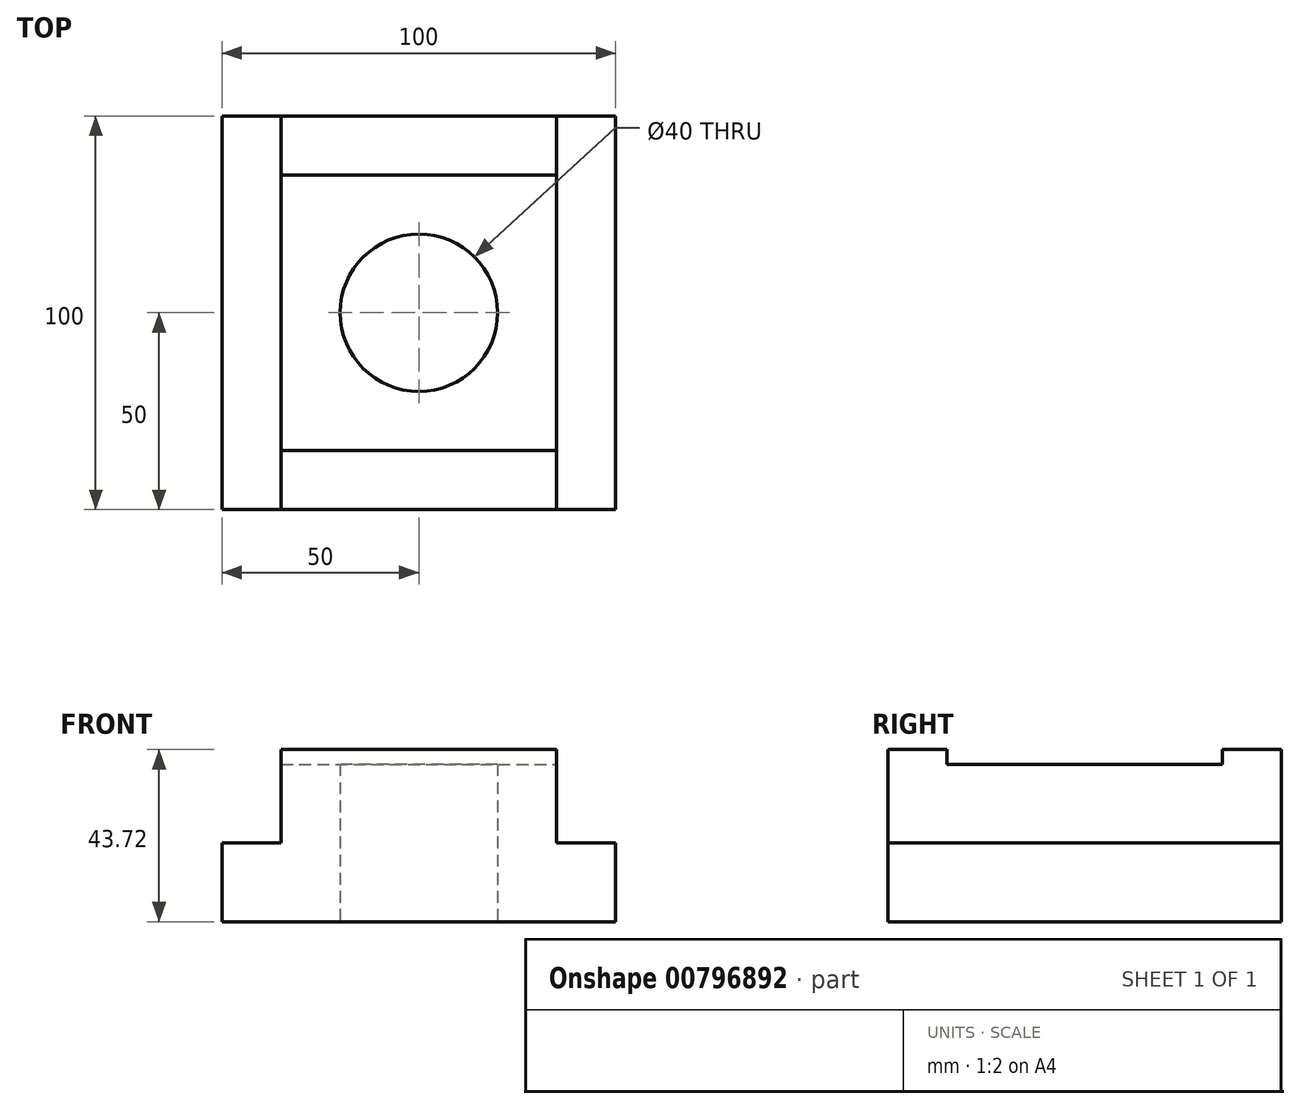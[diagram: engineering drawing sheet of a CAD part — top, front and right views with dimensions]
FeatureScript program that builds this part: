
annotation { "Feature Type Name" : "Feature", "Feature Type Description" : "" }
export const myFeature = defineFeature(function(context is Context, id is Id, definition is map)
    precondition{}
    {
        {
            var Q0;
            Q0=qCreatedBy(makeId("Front.planeOp"),FACE);
            var sketch = newSketch(context, id + "F0", { "sketchPlane" : qUnion([Q0])});
            skLineSegment(sketch, "E0.bottom", {"start": v(0, 0) * mm, "end": v(100, 0) * mm});
            skLineSegment(sketch, "E0.top", {"start": v(0, 20) * mm, "end": v(100, 20) * mm});
            skLineSegment(sketch, "E0.left", {"start": v(0, 0) * mm, "end": v(0, 20) * mm});
            skLineSegment(sketch, "E0.right", {"start": v(100, 0) * mm, "end": v(100, 20) * mm});
            skLineSegment(sketch, "E1.bottom", {"start": v(15, 20) * mm, "end": v(85, 20) * mm});
            skLineSegment(sketch, "E1.top", {"start": v(15, 43.72) * mm, "end": v(85, 43.72) * mm});
            skLineSegment(sketch, "E1.left", {"start": v(15, 20) * mm, "end": v(15, 43.72) * mm});
            skLineSegment(sketch, "E1.right", {"start": v(85, 20) * mm, "end": v(85, 43.72) * mm});
            skSolve(sketch);
        }
        {
            var Q0;
            Q0=qCreatedBy(makeId("Top.planeOp"),FACE);
            var sketch = newSketch(context, id + "F1", { "sketchPlane" : qUnion([Q0])});
            skLineSegment(sketch, "E2.bottom", {"start": v(15, 85) * mm, "end": v(85, 85) * mm});
            skLineSegment(sketch, "E2.top", {"start": v(15, 15) * mm, "end": v(85, 15) * mm});
            skLineSegment(sketch, "E2.left", {"start": v(15, 85) * mm, "end": v(15, 15) * mm});
            skLineSegment(sketch, "E2.right", {"start": v(85, 85) * mm, "end": v(85, 15) * mm});
            skLineSegment(sketch, "E3.bottom", {"start": v(0, 100) * mm, "end": v(100, 100) * mm});
            skLineSegment(sketch, "E3.top", {"start": v(0, 0) * mm, "end": v(100, 0) * mm});
            skLineSegment(sketch, "E3.left", {"start": v(0, 100) * mm, "end": v(0, 0) * mm});
            skLineSegment(sketch, "E3.right", {"start": v(100, 100) * mm, "end": v(100, 0) * mm});
            skCircle(sketch, "E4", {"center": v(50, 50) * mm, "radius": 20 * mm});
            skPoint(sketch, "E4.centerSnap0", {"position": v(50, 85) * mm});
            skSolve(sketch);
        }
        {
            var Q0;
            Q0 = qSketchRegion(id + "F0", true);
            extrude(context, id + "F2", {"entities" : qUnion([Q0]), "oppositeDirection" : true, "depth" : 1000 * mm, "offsetDistance" : 25 * mm});
        }
        {
            var Q0;
            Q0 = qSketchRegion(id + "F1", true);
            extrude(context, id + "F3", {"entities" : qUnion([Q0]), "operationType" : NewBodyOperationType.INTERSECT, "depth" : 1000 * mm, "offsetDistance" : 25 * mm});
        }
        {
            var Q0;
            Q0=makeQuery(id+"F1.imprint","IMPRINT",FACE,{"disambiguationData":[TD([[makeQuery(id+"F1.imprint","IMPRINT",EDGE,{"derivedFrom":sQuery(id+"F1.wireOp",EDGE,"E2.bottom")}),-1.0]])]});
            extrude(context, id + "F4", {"entities" : qUnion([Q0]), "operationType" : NewBodyOperationType.ADD, "depth" : 40 * mm, "offsetDistance" : 25 * mm});
        }
    });
